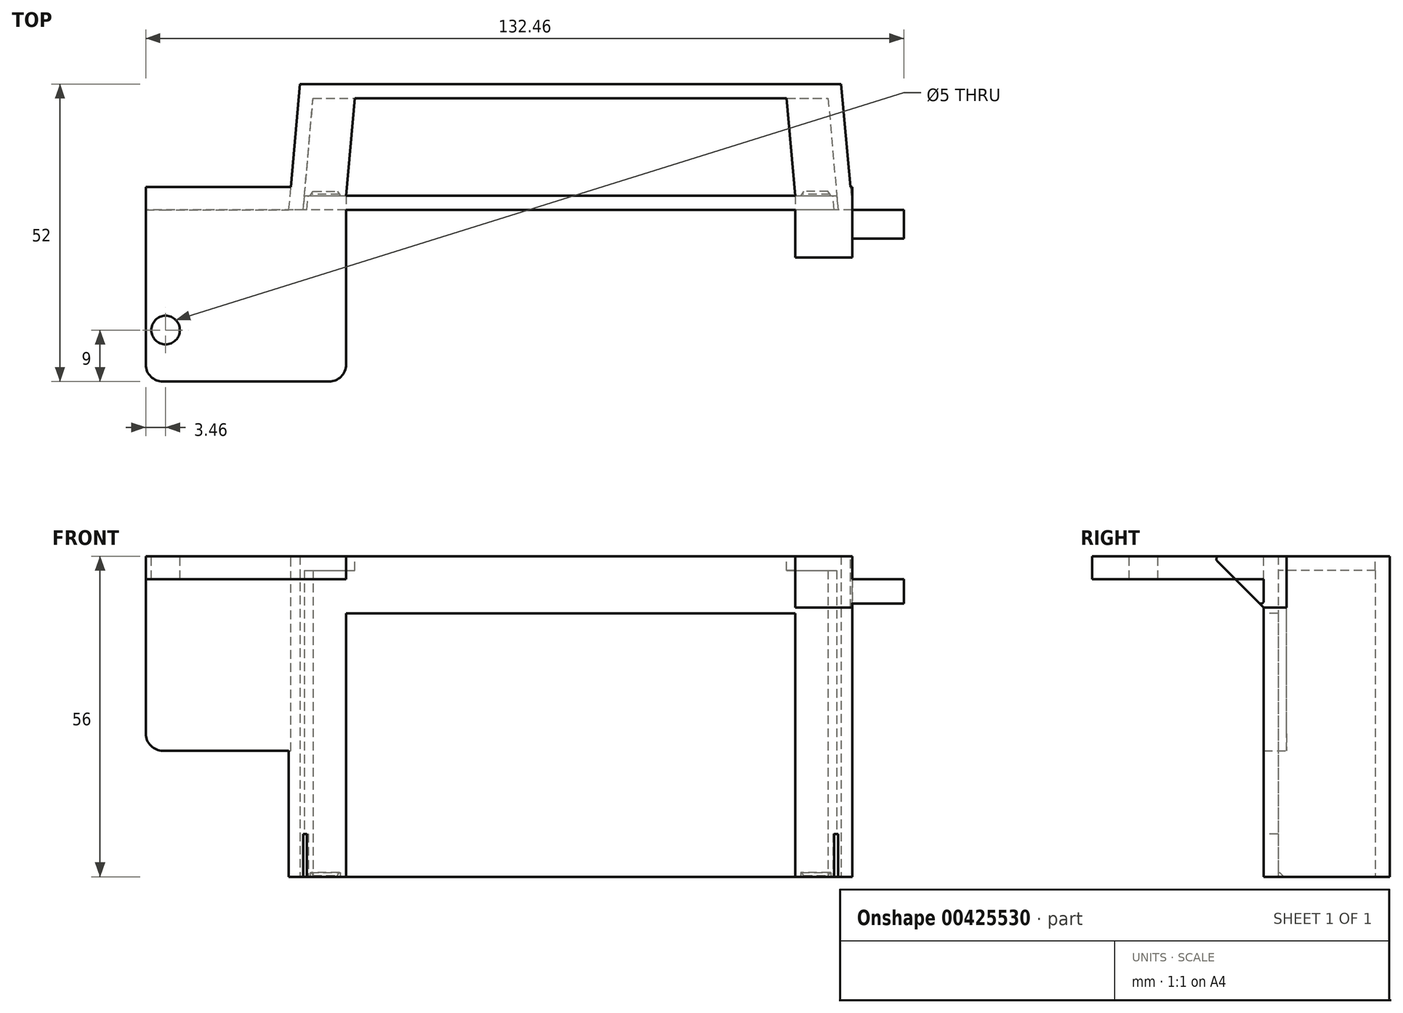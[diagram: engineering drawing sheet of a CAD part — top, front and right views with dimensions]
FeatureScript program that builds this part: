
annotation { "Feature Type Name" : "Feature", "Feature Type Description" : "" }
export const myFeature = defineFeature(function(context is Context, id is Id, definition is map)
    precondition{}
    {
        {
            var Q0;
            Q0=qCreatedBy(makeId("Top.planeOp"),FACE);
            var sketch = newSketch(context, id + "F0", { "sketchPlane" : qUnion([Q0])});
            skLineSegment(sketch, "E0", {"start": v(-46.5, -8.5) * mm, "end": v(-39.23, -8.5) * mm});
            skLineSegment(sketch, "E1", {"start": v(-45, 8.5) * mm, "end": v(45, 8.5) * mm});
            skLineSegment(sketch, "E2", {"start": v(-46.5, -8.5) * mm, "end": v(-45, 8.5) * mm});
            skLineSegment(sketch, "E3", {"start": v(45, 8.5) * mm, "end": v(46.5, -8.5) * mm});
            skLineSegment(sketch, "E4", {"start": v(-47.29, 11) * mm, "end": v(47.29, 11) * mm});
            skLineSegment(sketch, "E5", {"start": v(47.29, 11) * mm, "end": v(49.23, -11) * mm});
            skLineSegment(sketch, "E6", {"start": v(49.23, -11) * mm, "end": v(39.23, -11) * mm});
            skLineSegment(sketch, "E7", {"start": v(-49.23, -11) * mm, "end": v(-47.29, 11) * mm});
            skLineSegment(sketch, "E8", {"start": v(-39.23, -8.5) * mm, "end": v(-39.23, -11) * mm});
            skLineSegment(sketch, "E9.MirrorCS", {"start": v(39.23, -8.5) * mm, "end": v(39.23, -11) * mm});
            skLineSegment(sketch, "E10", {"start": v(39.23, -8.5) * mm, "end": v(46.5, -8.5) * mm});
            skLineSegment(sketch, "E11", {"start": v(-39.23, -11) * mm, "end": v(-49.23, -11) * mm});
            skSolve(sketch);
        }
        {
            var Q0;
            Q0 = qSketchRegion(id + "F0", true);
            extrude(context, id + "F1", {"entities" : qUnion([Q0]), "depth" : 56 * mm, "offsetDistance" : 25 * mm});
        }
        {
            var Q0;
            Q0=makeQuery(id+"F1.opExtrude","CAP_FACE",FACE,{"disambiguationData":[OSD([sQuery(id+"F0.wireOp",EDGE,"E0"),sQuery(id+"F0.wireOp",EDGE,"E1"),sQuery(id+"F0.wireOp",EDGE,"E2"),sQuery(id+"F0.wireOp",EDGE,"E3"),sQuery(id+"F0.wireOp",EDGE,"E4"),sQuery(id+"F0.wireOp",EDGE,"E5"),sQuery(id+"F0.wireOp",EDGE,"E6"),sQuery(id+"F0.wireOp",EDGE,"E7"),sQuery(id+"F0.wireOp",EDGE,"E8"),sQuery(id+"F0.wireOp",EDGE,"E9.MirrorCS"),sQuery(id+"F0.wireOp",EDGE,"E10"),sQuery(id+"F0.wireOp",EDGE,"E11")])],"isStart":false});
            var sketch = newSketch(context, id + "F2", { "sketchPlane" : qUnion([Q0])});
            skLineSegment(sketch, "E12", {"start": v(-39.23, -8.5) * mm, "end": v(-37.73, 8.5) * mm});
            skLineSegment(sketch, "E13", {"start": v(-37.73, 8.5) * mm, "end": v(-45, 8.5) * mm});
            skLineSegment(sketch, "E14", {"start": v(-45, 8.5) * mm, "end": v(-46.5, -8.5) * mm});
            skLineSegment(sketch, "E15", {"start": v(-46.5, -8.5) * mm, "end": v(-39.23, -8.5) * mm});
            skLineSegment(sketch, "E16.MirrorCS", {"start": v(45, 8.5) * mm, "end": v(46.5, -8.5) * mm});
            skLineSegment(sketch, "E17.MirrorCS", {"start": v(46.5, -8.5) * mm, "end": v(39.23, -8.5) * mm});
            skLineSegment(sketch, "E18.MirrorCS", {"start": v(37.73, 8.5) * mm, "end": v(45, 8.5) * mm});
            skLineSegment(sketch, "E19.MirrorCS", {"start": v(39.23, -8.5) * mm, "end": v(37.73, 8.5) * mm});
            skSolve(sketch);
        }
        {
            var Q0;
            Q0 = qSketchRegion(id + "F2", true);
            extrude(context, id + "F3", {"entities" : qUnion([Q0]), "operationType" : NewBodyOperationType.ADD, "oppositeDirection" : true, "depth" : 2.5 * mm, "offsetDistance" : 25 * mm});
        }
        {
            var Q0;
            Q0=makeQuery(id+"F1.opExtrude","CAP_FACE",FACE,{"disambiguationData":[OSD([sQuery(id+"F0.wireOp",EDGE,"E0"),sQuery(id+"F0.wireOp",EDGE,"E1"),sQuery(id+"F0.wireOp",EDGE,"E2"),sQuery(id+"F0.wireOp",EDGE,"E3"),sQuery(id+"F0.wireOp",EDGE,"E4"),sQuery(id+"F0.wireOp",EDGE,"E5"),sQuery(id+"F0.wireOp",EDGE,"E6"),sQuery(id+"F0.wireOp",EDGE,"E7"),sQuery(id+"F0.wireOp",EDGE,"E8"),sQuery(id+"F0.wireOp",EDGE,"E9.MirrorCS"),sQuery(id+"F0.wireOp",EDGE,"E10"),sQuery(id+"F0.wireOp",EDGE,"E11")])],"isStart":true});
            var sketch = newSketch(context, id + "F4", { "sketchPlane" : qUnion([Q0])});
            skLineSegment(sketch, "E20", {"start": v(-40.23, 8.5) * mm, "end": v(-45.5, 8.5) * mm});
            skLineSegment(sketch, "E21", {"start": v(-45.5, 8.5) * mm, "end": v(-45, 7.75) * mm});
            skLineSegment(sketch, "E22", {"start": v(-45, 7.75) * mm, "end": v(-40.73, 7.75) * mm});
            skLineSegment(sketch, "E23", {"start": v(-40.73, 7.75) * mm, "end": v(-40.23, 8.5) * mm});
            skPoint(sketch, "E24.orphan", {"position": v(-39.23, 8.5) * mm});
            skPoint(sketch, "E25.orphan", {"position": v(-46.5, 8.5) * mm});
            skLineSegment(sketch, "E26.MirrorCS", {"start": v(45.5, 8.5) * mm, "end": v(45, 7.75) * mm});
            skPoint(sketch, "E27.MirrorP", {"position": v(39.23, 8.5) * mm});
            skLineSegment(sketch, "E28.MirrorCS", {"start": v(40.73, 7.75) * mm, "end": v(40.23, 8.5) * mm});
            skLineSegment(sketch, "E29.MirrorCS", {"start": v(40.23, 8.5) * mm, "end": v(45.5, 8.5) * mm});
            skLineSegment(sketch, "E30.MirrorCS", {"start": v(45, 7.75) * mm, "end": v(40.73, 7.75) * mm});
            skPoint(sketch, "E31.MirrorP", {"position": v(46.5, 8.5) * mm});
            skSolve(sketch);
        }
        {
            var Q0;
            Q0 = qSketchRegion(id + "F4", true);
            extrude(context, id + "F5", {"entities" : qUnion([Q0]), "operationType" : NewBodyOperationType.ADD, "oppositeDirection" : true, "depth" : 0.75 * mm, "offsetDistance" : 25 * mm});
        }
        {
            var Q0;
            Q0=makeQuery(id+"F5.opExtrude","CAP_EDGE",EDGE,{"disambiguationData":[OSD([sQuery(id+"F4.wireOp",EDGE,"E30.MirrorCS")])],"isStart":false});
            chamfer(context, id + "F6", {"entities" : qUnion([Q0]), "width" : 0.5 * mm, "tangentPropagation" : true});
        }
        {
            var Q0;
            Q0=makeQuery(id+"F5.opExtrude","CAP_EDGE",EDGE,{"disambiguationData":[OSD([sQuery(id+"F4.wireOp",EDGE,"E22")])],"isStart":false});
            chamfer(context, id + "F7", {"entities" : qUnion([Q0]), "width" : 0.5 * mm, "tangentPropagation" : true});
        }
        {
            var Q0;
            Q0=makeQuery(id+"F5.boolean.opBoolean","MERGE",FACE,{"derivedFrom":[makeQuery(id+"F1.opExtrude","CAP_FACE",FACE,{"disambiguationData":[OSD([sQuery(id+"F0.wireOp",EDGE,"E0"),sQuery(id+"F0.wireOp",EDGE,"E1"),sQuery(id+"F0.wireOp",EDGE,"E2"),sQuery(id+"F0.wireOp",EDGE,"E3"),sQuery(id+"F0.wireOp",EDGE,"E4"),sQuery(id+"F0.wireOp",EDGE,"E5"),sQuery(id+"F0.wireOp",EDGE,"E6"),sQuery(id+"F0.wireOp",EDGE,"E7"),sQuery(id+"F0.wireOp",EDGE,"E8"),sQuery(id+"F0.wireOp",EDGE,"E9.MirrorCS"),sQuery(id+"F0.wireOp",EDGE,"E10"),sQuery(id+"F0.wireOp",EDGE,"E11")])],"isStart":true}),makeQuery(id+"F5.opExtrude","CAP_FACE",FACE,{"disambiguationData":[OSD([sQuery(id+"F4.wireOp",EDGE,"E20"),sQuery(id+"F4.wireOp",EDGE,"E21"),sQuery(id+"F4.wireOp",EDGE,"E22"),sQuery(id+"F4.wireOp",EDGE,"E23")])],"isStart":true}),makeQuery(id+"F5.opExtrude","CAP_FACE",FACE,{"disambiguationData":[OSD([sQuery(id+"F4.wireOp",EDGE,"E26.MirrorCS"),sQuery(id+"F4.wireOp",EDGE,"E28.MirrorCS"),sQuery(id+"F4.wireOp",EDGE,"E29.MirrorCS"),sQuery(id+"F4.wireOp",EDGE,"E30.MirrorCS")])],"isStart":true})]});
            var sketch = newSketch(context, id + "F8", { "sketchPlane" : qUnion([Q0])});
            skLineSegment(sketch, "E32", {"start": v(-46.5, 8.5) * mm, "end": v(-46.72, 11) * mm});
            skLineSegment(sketch, "E33", {"start": v(-46.72, 11) * mm, "end": v(-46.06, 11) * mm});
            skLineSegment(sketch, "E34", {"start": v(-46.06, 11) * mm, "end": v(-45.84, 8.5) * mm});
            skLineSegment(sketch, "E35", {"start": v(-45.84, 8.5) * mm, "end": v(-46.5, 8.5) * mm});
            skLineSegment(sketch, "E36.MirrorCS", {"start": v(46.72, 11) * mm, "end": v(46.06, 11) * mm});
            skLineSegment(sketch, "E37.MirrorCS", {"start": v(46.06, 11) * mm, "end": v(45.84, 8.5) * mm});
            skLineSegment(sketch, "E38.MirrorCS", {"start": v(46.5, 8.5) * mm, "end": v(46.72, 11) * mm});
            skLineSegment(sketch, "E39.MirrorCS", {"start": v(45.84, 8.5) * mm, "end": v(46.5, 8.5) * mm});
            skSolve(sketch);
        }
        {
            var Q0;
            Q0 = qSketchRegion(id + "F8", true);
            extrude(context, id + "F9", {"entities" : qUnion([Q0]), "operationType" : NewBodyOperationType.REMOVE, "oppositeDirection" : true, "depth" : 7.5 * mm, "offsetDistance" : 25 * mm});
        }
        {
            var Q0;
            Q0=makeQuery(id+"F3.boolean.opBoolean","MERGE",FACE,{"derivedFrom":[makeQuery(id+"F1.opExtrude","CAP_FACE",FACE,{"disambiguationData":[OSD([sQuery(id+"F0.wireOp",EDGE,"E0"),sQuery(id+"F0.wireOp",EDGE,"E1"),sQuery(id+"F0.wireOp",EDGE,"E2"),sQuery(id+"F0.wireOp",EDGE,"E3"),sQuery(id+"F0.wireOp",EDGE,"E4"),sQuery(id+"F0.wireOp",EDGE,"E5"),sQuery(id+"F0.wireOp",EDGE,"E6"),sQuery(id+"F0.wireOp",EDGE,"E7"),sQuery(id+"F0.wireOp",EDGE,"E8"),sQuery(id+"F0.wireOp",EDGE,"E9.MirrorCS"),sQuery(id+"F0.wireOp",EDGE,"E10"),sQuery(id+"F0.wireOp",EDGE,"E11")])],"isStart":false}),makeQuery(id+"F3.opExtrude","CAP_FACE",FACE,{"disambiguationData":[OSD([sQuery(id+"F2.wireOp",EDGE,"E12"),sQuery(id+"F2.wireOp",EDGE,"E13"),sQuery(id+"F2.wireOp",EDGE,"E14"),sQuery(id+"F2.wireOp",EDGE,"E15")])],"isStart":true}),makeQuery(id+"F3.opExtrude","CAP_FACE",FACE,{"disambiguationData":[OSD([sQuery(id+"F2.wireOp",EDGE,"E16.MirrorCS"),sQuery(id+"F2.wireOp",EDGE,"E17.MirrorCS"),sQuery(id+"F2.wireOp",EDGE,"E18.MirrorCS"),sQuery(id+"F2.wireOp",EDGE,"E19.MirrorCS")])],"isStart":true})]});
            var sketch = newSketch(context, id + "F10", { "sketchPlane" : qUnion([Q0])});
            skLineSegment(sketch, "E40", {"start": v(-74.23, -11) * mm, "end": v(-74.23, -7) * mm});
            skLineSegment(sketch, "E41", {"start": v(-74.23, -7) * mm, "end": v(-48.88, -7) * mm});
            skLineSegment(sketch, "E42", {"start": v(-39.23, -11) * mm, "end": v(-39.23, -41) * mm});
            skLineSegment(sketch, "E43", {"start": v(-39.23, -41) * mm, "end": v(-74.23, -41) * mm});
            skLineSegment(sketch, "E44", {"start": v(-74.23, -41) * mm, "end": v(-74.23, -11) * mm});
            skLineSegment(sketch, "E45", {"start": v(-48.88, -7) * mm, "end": v(-49.23, -11) * mm});
            skLineSegment(sketch, "E46", {"start": v(-49.23, -11) * mm, "end": v(-39.23, -11) * mm});
            skLineSegment(sketch, "E47", {"start": v(39.23, -11) * mm, "end": v(49.23, -11) * mm});
            skLineSegment(sketch, "E48", {"start": v(58.23, -7) * mm, "end": v(58.23, -11) * mm});
            skLineSegment(sketch, "E49", {"start": v(58.23, -11) * mm, "end": v(58.23, -20) * mm});
            skLineSegment(sketch, "E50", {"start": v(58.23, -20) * mm, "end": v(39.23, -20) * mm});
            skLineSegment(sketch, "E51", {"start": v(39.23, -20) * mm, "end": v(39.23, -11) * mm});
            skLineSegment(sketch, "E52", {"start": v(48.88, -7) * mm, "end": v(58.23, -7) * mm});
            skLineSegment(sketch, "E53", {"start": v(49.23, -11) * mm, "end": v(48.88, -7) * mm});
            skSolve(sketch);
        }
        {
            var Q0;
            Q0 = qSketchRegion(id + "F10", true);
            extrude(context, id + "F11", {"entities" : qUnion([Q0]), "operationType" : NewBodyOperationType.ADD, "oppositeDirection" : true, "depth" : 4 * mm, "offsetDistance" : 25 * mm});
        }
        {
            var Q0;
            Q0=makeQuery(id+"F11.opExtrude","CAP_FACE",FACE,{"disambiguationData":[OSD([sQuery(id+"F10.wireOp",EDGE,"E40"),sQuery(id+"F10.wireOp",EDGE,"E41"),sQuery(id+"F10.wireOp",EDGE,"E42"),sQuery(id+"F10.wireOp",EDGE,"E43"),sQuery(id+"F10.wireOp",EDGE,"E44"),sQuery(id+"F10.wireOp",EDGE,"E45"),sQuery(id+"F10.wireOp",EDGE,"E46")])],"isStart":false});
            var sketch = newSketch(context, id + "F12", { "sketchPlane" : qUnion([Q0])});
            skLineSegment(sketch, "E54", {"start": v(-48.88, 7) * mm, "end": v(-74.23, 7) * mm});
            skLineSegment(sketch, "E55", {"start": v(-74.23, 7) * mm, "end": v(-74.23, 11) * mm});
            skLineSegment(sketch, "E56", {"start": v(-74.23, 11) * mm, "end": v(-49.23, 11) * mm});
            skLineSegment(sketch, "E57", {"start": v(-49.23, 11) * mm, "end": v(-48.88, 7) * mm});
            skSolve(sketch);
        }
        {
            var Q0;
            Q0 = qSketchRegion(id + "F12", true);
            extrude(context, id + "F13", {"entities" : qUnion([Q0]), "operationType" : NewBodyOperationType.ADD, "depth" : 30 * mm, "offsetDistance" : 25 * mm});
        }
        {
            var Q0;
            Q0=makeQuery(id+"F11.opExtrude","CAP_FACE",FACE,{"disambiguationData":[OSD([sQuery(id+"F10.wireOp",EDGE,"E47"),sQuery(id+"F10.wireOp",EDGE,"E48"),sQuery(id+"F10.wireOp",EDGE,"E49"),sQuery(id+"F10.wireOp",EDGE,"E50"),sQuery(id+"F10.wireOp",EDGE,"E51"),sQuery(id+"F10.wireOp",EDGE,"E52"),sQuery(id+"F10.wireOp",EDGE,"E53")])],"isStart":false});
            var sketch = newSketch(context, id + "F14", { "sketchPlane" : qUnion([Q0])});
            skLineSegment(sketch, "E58", {"start": v(39.23, 20) * mm, "end": v(58.23, 20) * mm});
            skLineSegment(sketch, "E59", {"start": v(58.23, 20) * mm, "end": v(58.23, 7) * mm});
            skLineSegment(sketch, "E60", {"start": v(58.23, 7) * mm, "end": v(48.88, 7) * mm});
            skLineSegment(sketch, "E61", {"start": v(48.88, 7) * mm, "end": v(49.23, 11) * mm});
            skLineSegment(sketch, "E62", {"start": v(49.23, 11) * mm, "end": v(39.23, 11) * mm});
            skLineSegment(sketch, "E63", {"start": v(39.23, 11) * mm, "end": v(39.23, 20) * mm});
            skSolve(sketch);
        }
        {
            var Q0;
            Q0 = qSketchRegion(id + "F14", true);
            extrude(context, id + "F15", {"entities" : qUnion([Q0]), "operationType" : NewBodyOperationType.ADD, "depth" : 5 * mm, "offsetDistance" : 25 * mm});
        }
        {
            var Q0;
            Q0=makeQuery(id+"F15.boolean.opBoolean","MERGE",FACE,{"derivedFrom":[makeQuery(id+"F11.opExtrude","SWEPT_FACE",FACE,{"disambiguationData":[OSD([sQuery(id+"F10.wireOp",EDGE,"E48"),sQuery(id+"F10.wireOp",EDGE,"E49")])]}),makeQuery(id+"F15.opExtrude","SWEPT_FACE",FACE,{"disambiguationData":[OSD([sQuery(id+"F14.wireOp",EDGE,"E59")])]})]});
            var sketch = newSketch(context, id + "F16", { "sketchPlane" : qUnion([Q0])});
            skLineSegment(sketch, "E64", {"start": v(-20, 56) * mm, "end": v(-20, 47) * mm});
            skLineSegment(sketch, "E65", {"start": v(-20, 47) * mm, "end": v(-7, 47) * mm});
            skLineSegment(sketch, "E66", {"start": v(-11, 56) * mm, "end": v(-11, 47) * mm});
            skLineSegment(sketch, "E67", {"start": v(-11, 47) * mm, "end": v(-20, 56) * mm});
            skLineSegment(sketch, "E68", {"start": v(-7, 47) * mm, "end": v(-7, 56) * mm});
            skLineSegment(sketch, "E69", {"start": v(-7, 56) * mm, "end": v(-11, 56) * mm});
            skSolve(sketch);
        }
        {
            var Q0;
            Q0 = qSketchRegion(id + "F16", true);
            extrude(context, id + "F17", {"entities" : qUnion([Q0]), "operationType" : NewBodyOperationType.REMOVE, "oppositeDirection" : true, "depth" : 9 * mm, "offsetDistance" : 25 * mm});
        }
        {
            var Q0;
            Q0=makeQuery(id+"F17.boolean.opBoolean","COPY",FACE,{"derivedFrom":makeQuery(id+"F17.opExtrude","CAP_FACE",FACE,{"disambiguationData":[OSD([sQuery(id+"F16.wireOp",EDGE,"E64"),sQuery(id+"F16.wireOp",EDGE,"E65"),sQuery(id+"F16.wireOp",EDGE,"E67")])],"isStart":false})});
            var sketch = newSketch(context, id + "F18", { "sketchPlane" : qUnion([Q0])});
            skLineSegment(sketch, "E70", {"start": v(-20, 56) * mm, "end": v(-11, 47) * mm});
            skLineSegment(sketch, "E71", {"start": v(-11, 47) * mm, "end": v(-20, 47) * mm});
            skLineSegment(sketch, "E72", {"start": v(-20, 47) * mm, "end": v(-20, 56) * mm});
            skSolve(sketch);
        }
        {
            var Q0;
            Q0 = qSketchRegion(id + "F18", true);
            extrude(context, id + "F19", {"entities" : qUnion([Q0]), "operationType" : NewBodyOperationType.REMOVE, "oppositeDirection" : true, "depth" : 10 * mm, "offsetDistance" : 25 * mm});
        }
        {
            var Q0;
            {var subQ0=makeQuery(id+"F11.opExtrude","CAP_EDGE",EDGE,{"disambiguationData":[OSD([sQuery(id+"F10.wireOp",EDGE,"E50")])],"isStart":true});Q0=makeQuery(id+"F19.boolean.opBoolean","MERGE",EDGE,{"derivedFrom":[makeQuery(id+"F17.boolean.opBoolean","MERGE",EDGE,{"derivedFrom":[subQ0],"fromTools":[makeQuery(id+"F17.opExtrude","SWEPT_EDGE",EDGE,{"disambiguationData":[OSD([sQuery(id+"F10.wireOp",EDGE,"E48"),sQuery(id+"F10.wireOp",EDGE,"E49"),sQuery(id+"F16.wireOp",EDGE,"E64"),sQuery(id+"F16.wireOp",EDGE,"E67")])]})]}),makeQuery(id+"F17.boolean.opBoolean","SPLIT",EDGE,{"derivedFrom":subQ0})],"fromTools":[makeQuery(id+"F19.opExtrude","SWEPT_EDGE",EDGE,{"disambiguationData":[OSD([sQuery(id+"F18.wireOp",EDGE,"E70"),sQuery(id+"F18.wireOp",EDGE,"E72")])]})]});}
            var Q1;
            {var subQ0=sQuery(id+"F16.wireOp",EDGE,"E67");var subQ1=sQuery(id+"F16.wireOp",EDGE,"E66");var subQ2=sQuery(id+"F16.wireOp",EDGE,"E65");Q1=makeQuery(id+"F17.boolean.opBoolean","MERGE",EDGE,{"derivedFrom":[],"fromTools":[makeQuery(id+"F17.opExtrude","SWEPT_EDGE",EDGE,{"disambiguationData":[OSD([subQ2,subQ1,subQ0]),OD(0.0)]}),makeQuery(id+"F17.opExtrude","SWEPT_EDGE",EDGE,{"disambiguationData":[OSD([subQ2,subQ1,subQ0]),OD(1.0)]})]});}
            var Q2;
            Q2=makeQuery(id+"F17.boolean.opBoolean","COPY",EDGE,{"derivedFrom":makeQuery(id+"F17.opExtrude","SWEPT_EDGE",EDGE,{"disambiguationData":[OSD([sQuery(id+"F10.wireOp",EDGE,"E48"),sQuery(id+"F10.wireOp",EDGE,"E49"),sQuery(id+"F16.wireOp",EDGE,"E66"),sQuery(id+"F16.wireOp",EDGE,"E69")])]})});
            fillet(context, id + "F20", {"entities" : qUnion([Q0, Q1, Q2]), "tangentPropagation" : true, "radius" : 0.5 * mm, "defaultsChanged" : false, "vertexSettings" : [], "allowEdgeOverflow" : false});
        }
        {
            var Q0;
            Q0=makeQuery(id+"F11.boolean.opBoolean","MERGE",FACE,{"derivedFrom":[makeQuery(id+"F3.boolean.opBoolean","MERGE",FACE,{"derivedFrom":[makeQuery(id+"F1.opExtrude","CAP_FACE",FACE,{"disambiguationData":[OSD([sQuery(id+"F0.wireOp",EDGE,"E0"),sQuery(id+"F0.wireOp",EDGE,"E1"),sQuery(id+"F0.wireOp",EDGE,"E2"),sQuery(id+"F0.wireOp",EDGE,"E3"),sQuery(id+"F0.wireOp",EDGE,"E4"),sQuery(id+"F0.wireOp",EDGE,"E5"),sQuery(id+"F0.wireOp",EDGE,"E6"),sQuery(id+"F0.wireOp",EDGE,"E7"),sQuery(id+"F0.wireOp",EDGE,"E8"),sQuery(id+"F0.wireOp",EDGE,"E9.MirrorCS"),sQuery(id+"F0.wireOp",EDGE,"E10"),sQuery(id+"F0.wireOp",EDGE,"E11")])],"isStart":false}),makeQuery(id+"F3.opExtrude","CAP_FACE",FACE,{"disambiguationData":[OSD([sQuery(id+"F2.wireOp",EDGE,"E12"),sQuery(id+"F2.wireOp",EDGE,"E13"),sQuery(id+"F2.wireOp",EDGE,"E14"),sQuery(id+"F2.wireOp",EDGE,"E15")])],"isStart":true}),makeQuery(id+"F3.opExtrude","CAP_FACE",FACE,{"disambiguationData":[OSD([sQuery(id+"F2.wireOp",EDGE,"E16.MirrorCS"),sQuery(id+"F2.wireOp",EDGE,"E17.MirrorCS"),sQuery(id+"F2.wireOp",EDGE,"E18.MirrorCS"),sQuery(id+"F2.wireOp",EDGE,"E19.MirrorCS")])],"isStart":true})]}),makeQuery(id+"F11.opExtrude","CAP_FACE",FACE,{"disambiguationData":[OSD([sQuery(id+"F10.wireOp",EDGE,"E40"),sQuery(id+"F10.wireOp",EDGE,"E41"),sQuery(id+"F10.wireOp",EDGE,"E42"),sQuery(id+"F10.wireOp",EDGE,"E43"),sQuery(id+"F10.wireOp",EDGE,"E44"),sQuery(id+"F10.wireOp",EDGE,"E45"),sQuery(id+"F10.wireOp",EDGE,"E46")])],"isStart":true}),makeQuery(id+"F11.opExtrude","CAP_FACE",FACE,{"disambiguationData":[OSD([sQuery(id+"F10.wireOp",EDGE,"E47"),sQuery(id+"F10.wireOp",EDGE,"E48"),sQuery(id+"F10.wireOp",EDGE,"E49"),sQuery(id+"F10.wireOp",EDGE,"E50"),sQuery(id+"F10.wireOp",EDGE,"E51"),sQuery(id+"F10.wireOp",EDGE,"E52"),sQuery(id+"F10.wireOp",EDGE,"E53")])],"isStart":true})]});
            var sketch = newSketch(context, id + "F21", { "sketchPlane" : qUnion([Q0])});
            skLineSegment(sketch, "E73.bottom", {"start": v(-39.23, -11) * mm, "end": v(39.23, -11) * mm});
            skLineSegment(sketch, "E73.top", {"start": v(-39.23, -8.5) * mm, "end": v(39.23, -8.5) * mm});
            skLineSegment(sketch, "E73.left", {"start": v(-39.23, -11) * mm, "end": v(-39.23, -8.5) * mm});
            skLineSegment(sketch, "E73.right", {"start": v(39.23, -11) * mm, "end": v(39.23, -8.5) * mm});
            skSolve(sketch);
        }
        {
            var Q0;
            Q0 = qSketchRegion(id + "F21", true);
            extrude(context, id + "F22", {"entities" : qUnion([Q0]), "operationType" : NewBodyOperationType.ADD, "oppositeDirection" : true, "depth" : 10 * mm, "offsetDistance" : 25 * mm});
        }
        {
            var Q0;
            Q0=makeQuery(id+"F22.boolean.opBoolean","MERGE",FACE,{"derivedFrom":[makeQuery(id+"F11.boolean.opBoolean","MERGE",FACE,{"derivedFrom":[makeQuery(id+"F3.boolean.opBoolean","MERGE",FACE,{"derivedFrom":[makeQuery(id+"F1.opExtrude","CAP_FACE",FACE,{"disambiguationData":[OSD([sQuery(id+"F0.wireOp",EDGE,"E0"),sQuery(id+"F0.wireOp",EDGE,"E1"),sQuery(id+"F0.wireOp",EDGE,"E2"),sQuery(id+"F0.wireOp",EDGE,"E3"),sQuery(id+"F0.wireOp",EDGE,"E4"),sQuery(id+"F0.wireOp",EDGE,"E5"),sQuery(id+"F0.wireOp",EDGE,"E6"),sQuery(id+"F0.wireOp",EDGE,"E7"),sQuery(id+"F0.wireOp",EDGE,"E8"),sQuery(id+"F0.wireOp",EDGE,"E9.MirrorCS"),sQuery(id+"F0.wireOp",EDGE,"E10"),sQuery(id+"F0.wireOp",EDGE,"E11")])],"isStart":false}),makeQuery(id+"F3.opExtrude","CAP_FACE",FACE,{"disambiguationData":[OSD([sQuery(id+"F2.wireOp",EDGE,"E12"),sQuery(id+"F2.wireOp",EDGE,"E13"),sQuery(id+"F2.wireOp",EDGE,"E14"),sQuery(id+"F2.wireOp",EDGE,"E15")])],"isStart":true}),makeQuery(id+"F3.opExtrude","CAP_FACE",FACE,{"disambiguationData":[OSD([sQuery(id+"F2.wireOp",EDGE,"E16.MirrorCS"),sQuery(id+"F2.wireOp",EDGE,"E17.MirrorCS"),sQuery(id+"F2.wireOp",EDGE,"E18.MirrorCS"),sQuery(id+"F2.wireOp",EDGE,"E19.MirrorCS")])],"isStart":true})]}),makeQuery(id+"F11.opExtrude","CAP_FACE",FACE,{"disambiguationData":[OSD([sQuery(id+"F10.wireOp",EDGE,"E40"),sQuery(id+"F10.wireOp",EDGE,"E41"),sQuery(id+"F10.wireOp",EDGE,"E42"),sQuery(id+"F10.wireOp",EDGE,"E43"),sQuery(id+"F10.wireOp",EDGE,"E44"),sQuery(id+"F10.wireOp",EDGE,"E45"),sQuery(id+"F10.wireOp",EDGE,"E46")])],"isStart":true}),makeQuery(id+"F11.opExtrude","CAP_FACE",FACE,{"disambiguationData":[OSD([sQuery(id+"F10.wireOp",EDGE,"E47"),sQuery(id+"F10.wireOp",EDGE,"E48"),sQuery(id+"F10.wireOp",EDGE,"E49"),sQuery(id+"F10.wireOp",EDGE,"E50"),sQuery(id+"F10.wireOp",EDGE,"E51"),sQuery(id+"F10.wireOp",EDGE,"E52"),sQuery(id+"F10.wireOp",EDGE,"E53")])],"isStart":true})]}),makeQuery(id+"F22.opExtrude","CAP_FACE",FACE,{"disambiguationData":[OSD([sQuery(id+"F21.wireOp",EDGE,"E73.bottom"),sQuery(id+"F21.wireOp",EDGE,"E73.top"),sQuery(id+"F21.wireOp",EDGE,"E73.left"),sQuery(id+"F21.wireOp",EDGE,"E73.right")])],"isStart":true})]});
            var sketch = newSketch(context, id + "F23", { "sketchPlane" : qUnion([Q0])});
            skCircle(sketch, "E74", {"center": v(-70.77, -32) * mm, "radius": 2.5 * mm});
            skSolve(sketch);
        }
        {
            var Q0;
            Q0 = qSketchRegion(id + "F23", true);
            extrude(context, id + "F24", {"entities" : qUnion([Q0]), "operationType" : NewBodyOperationType.REMOVE, "oppositeDirection" : true, "depth" : 4 * mm, "offsetDistance" : 25 * mm});
        }
        {
            var Q0;
            Q0=makeQuery(id+"F11.opExtrude","SWEPT_EDGE",EDGE,{"disambiguationData":[OSD([sQuery(id+"F10.wireOp",EDGE,"E43"),sQuery(id+"F10.wireOp",EDGE,"E44")])]});
            var Q1;
            Q1=makeQuery(id+"F11.opExtrude","SWEPT_EDGE",EDGE,{"disambiguationData":[OSD([sQuery(id+"F10.wireOp",EDGE,"E42"),sQuery(id+"F10.wireOp",EDGE,"E43")])]});
            var Q2;
            Q2=makeQuery(id+"F13.opExtrude","CAP_EDGE",EDGE,{"disambiguationData":[OSD([sQuery(id+"F12.wireOp",EDGE,"E55")])],"isStart":false});
            var Q3;
            Q3=makeQuery(id+"F13.opExtrude","CAP_EDGE",EDGE,{"disambiguationData":[OSD([sQuery(id+"F12.wireOp",EDGE,"E57")])],"isStart":false});
            var Q4;
            Q4=makeQuery(id+"F22.opExtrude","SWEPT_EDGE",EDGE,{"disambiguationData":[OSD([sQuery(id+"F0.wireOp",EDGE,"E8"),sQuery(id+"F10.wireOp",EDGE,"E42"),sQuery(id+"F21.wireOp",EDGE,"E73.bottom"),sQuery(id+"F21.wireOp",EDGE,"E73.left")])]});
            fillet(context, id + "F25", {"entities" : qUnion([Q0, Q1, Q2, Q3, Q4]), "tangentPropagation" : true, "radius" : 3 * mm, "defaultsChanged" : false, "vertexSettings" : [], "allowEdgeOverflow" : false});
        }
        {
            var Q0;
            Q0=makeQuery(id+"F15.boolean.opBoolean","MERGE",FACE,{"derivedFrom":[makeQuery(id+"F11.opExtrude","SWEPT_FACE",FACE,{"disambiguationData":[OSD([sQuery(id+"F10.wireOp",EDGE,"E48"),sQuery(id+"F10.wireOp",EDGE,"E49")])]}),makeQuery(id+"F15.opExtrude","SWEPT_FACE",FACE,{"disambiguationData":[OSD([sQuery(id+"F14.wireOp",EDGE,"E59")])]})]});
            var sketch = newSketch(context, id + "F26", { "sketchPlane" : qUnion([Q0])});
            skLineSegment(sketch, "E75", {"start": v(-11, 56) * mm, "end": v(-20, 56) * mm});
            skLineSegment(sketch, "E76", {"start": v(-20, 56) * mm, "end": v(-16, 52) * mm});
            skLineSegment(sketch, "E77", {"start": v(-11, 52) * mm, "end": v(-11, 56) * mm});
            skLineSegment(sketch, "E78.0", {"start": v(-11, 52) * mm, "end": v(-16, 52) * mm});
            skSolve(sketch);
        }
        {
            var Q0;
            Q0 = qSketchRegion(id + "F26", true);
            extrude(context, id + "F27", {"entities" : qUnion([Q0]), "operationType" : NewBodyOperationType.REMOVE, "oppositeDirection" : true, "depth" : 9 * mm, "offsetDistance" : 25 * mm});
        }
    });
